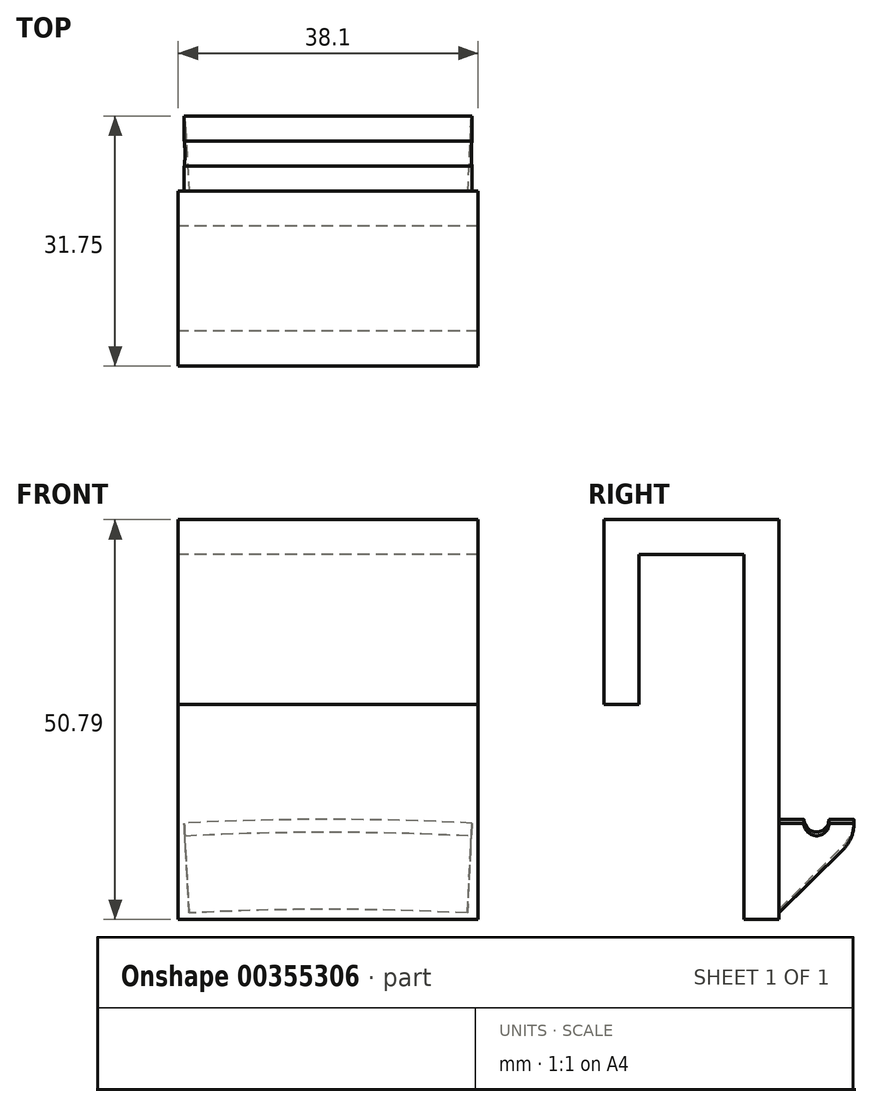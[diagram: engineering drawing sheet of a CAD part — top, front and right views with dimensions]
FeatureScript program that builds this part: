
annotation { "Feature Type Name" : "Feature", "Feature Type Description" : "" }
export const myFeature = defineFeature(function(context is Context, id is Id, definition is map)
    precondition{}
    {
        {
            var Q0;
            Q0=qCreatedBy(makeId("Right.planeOp"),FACE);
            var sketch = newSketch(context, id + "F0", { "sketchPlane" : qUnion([Q0])});
            skLineSegment(sketch, "E0.bottom", {"start": v(0, 0) * mm, "end": v(4.45, 0) * mm});
            skLineSegment(sketch, "E0.top", {"start": v(0, 23.5) * mm, "end": v(4.44, 23.5) * mm});
            skLineSegment(sketch, "E0.left", {"start": v(0, 0) * mm, "end": v(0, 23.5) * mm});
            skLineSegment(sketch, "E0.right", {"start": v(4.45, 0) * mm, "end": v(4.45, 19.05) * mm});
            skLineSegment(sketch, "E1.bottom", {"start": v(0, 23.5) * mm, "end": v(22.23, 23.5) * mm});
            skLineSegment(sketch, "E1.top", {"start": v(4.45, 19.05) * mm, "end": v(17.78, 19.05) * mm});
            skLineSegment(sketch, "E1.left", {"start": v(0, 23.5) * mm, "end": v(0, 19.05) * mm});
            skLineSegment(sketch, "E1.right", {"start": v(22.23, 23.5) * mm, "end": v(22.23, 19.05) * mm});
            skLineSegment(sketch, "E2.bottom", {"start": v(22.23, 23.5) * mm, "end": v(17.78, 23.5) * mm});
            skLineSegment(sketch, "E2.top", {"start": v(22.23, -27.3) * mm, "end": v(17.78, -27.3) * mm});
            skLineSegment(sketch, "E2.left", {"start": v(22.22, 23.5) * mm, "end": v(22.23, -27.3) * mm});
            skLineSegment(sketch, "E2.right", {"start": v(17.78, 19.05) * mm, "end": v(17.78, -27.3) * mm});
            skSolve(sketch);
        }
        {
            var Q0;
            Q0 = qSketchRegion(id + "F0", true);
            extrude(context, id + "F1", {"entities" : qUnion([Q0]), "endBound" : BoundingType.SYMMETRIC, "depth" : 38.1 * mm});
        }
        {
            var Q0;
            Q0=qCreatedBy(makeId("Right.planeOp"),FACE);
            var sketch = newSketch(context, id + "F2", { "sketchPlane" : qUnion([Q0])});
            skLineSegment(sketch, "E3", {"start": v(22.23, -14.6) * mm, "end": v(22.23, -14.6) * mm});
            skArc(sketch, "E4", {"start": v(25.4, -14.6) * mm, "mid": v(26.99, -16.2) * mm, "end": v(28.58, -14.6) * mm});
            skLineSegment(sketch, "E5", {"start": v(22.23, -14.6) * mm, "end": v(25.4, -14.6) * mm});
            skLineSegment(sketch, "E6.trimOffspring", {"start": v(28.58, -14.6) * mm, "end": v(31.75, -14.6) * mm});
            skLineSegment(sketch, "E7", {"start": v(22.23, -26.04) * mm, "end": v(22.23, -14.6) * mm});
            skArc(sketch, "E8.trimOffspring", {"start": v(30.34, -17.99) * mm, "mid": v(31.38, -16.44) * mm, "end": v(31.75, -14.6) * mm});
            skLineSegment(sketch, "E9", {"start": v(30.34, -17.99) * mm, "end": v(22.23, -26.04) * mm});
            skSolve(sketch);
        }
        {
            var Q0;
            Q0=qCreatedBy(makeId("Right.planeOp"),FACE);
            var sketch = newSketch(context, id + "F3", { "sketchPlane" : qUnion([Q0])});
            skLineSegment(sketch, "E10", {"start": v(201.1, -363.86) * mm, "end": v(0, -363.86) * mm, "construction": true});
            skSolve(sketch);
        }
        {
            var Q0;
            Q0=makeQuery(id+"F2.imprint","IMPRINT",FACE,{"disambiguationData":[TD([[makeQuery(id+"F2.imprint","IMPRINT",EDGE,{"derivedFrom":sQuery(id+"F2.wireOp",EDGE,"E4")}),-1.0]])]});
            var Q1;
            Q1=sQuery(id+"F3.wireOp",EDGE,"E10");
            revolve(context, id + "F4", {"entities" : qUnion([Q0]), "axis" : qUnion([Q1]), "revolveType" : RevolveType.SYMMETRIC, "angle" : 6 * degree});
        }
    });
